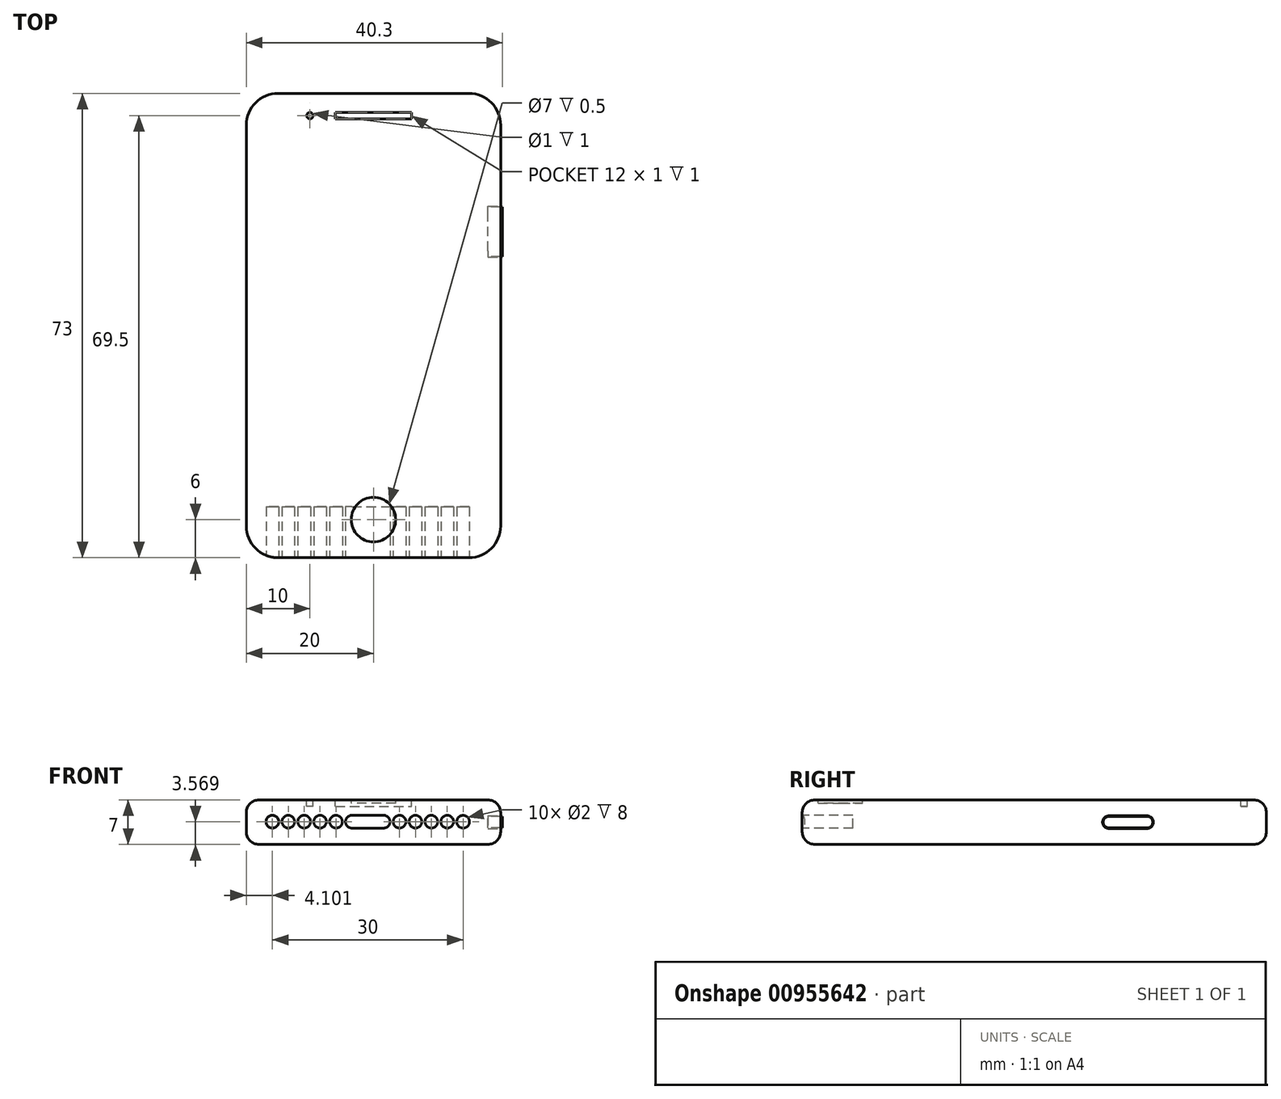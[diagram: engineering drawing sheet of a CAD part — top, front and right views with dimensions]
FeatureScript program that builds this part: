
annotation { "Feature Type Name" : "Feature", "Feature Type Description" : "" }
export const myFeature = defineFeature(function(context is Context, id is Id, definition is map)
    precondition{}
    {
        {
            var Q0;
            Q0=qCreatedBy(makeId("Top.planeOp"),FACE);
            var sketch = newSketch(context, id + "F0", { "sketchPlane" : qUnion([Q0])});
            skLineSegment(sketch, "E0.bottom", {"start": v(0, 0) * mm, "end": v(40, 0) * mm});
            skLineSegment(sketch, "E0.top", {"start": v(0, 73) * mm, "end": v(40, 73) * mm});
            skLineSegment(sketch, "E0.left", {"start": v(0, 0) * mm, "end": v(0, 73) * mm});
            skLineSegment(sketch, "E0.right", {"start": v(40, 0) * mm, "end": v(40, 73) * mm});
            skSolve(sketch);
        }
        {
            var Q0;
            Q0=makeQuery(id+"F0.imprint","IMPRINT",FACE,{"disambiguationData":[TD([[makeQuery(id+"F0.imprint","IMPRINT",EDGE,{"derivedFrom":sQuery(id+"F0.wireOp",EDGE,"E0.bottom")}),1.0]])]});
            extrude(context, id + "F1", {"entities" : qUnion([Q0]), "depth" : 7 * mm, "offsetDistance" : 25 * mm});
        }
        {
            var Q0;
            Q0=makeQuery(id+"F1.opExtrude","SWEPT_FACE",FACE,{"disambiguationData":[OSD([sQuery(id+"F0.wireOp",EDGE,"E0.bottom")])]});
            var sketch = newSketch(context, id + "F2", { "sketchPlane" : qUnion([Q0])});
            skLineSegment(sketch, "E1", {"start": v(0, 3.5) * mm, "end": v(40, 3.5) * mm});
            skSolve(sketch);
        }
        {
            var Q0;
            {var subQ0=sQuery(id+"F2.wireOp",EDGE,"E1");Q0=makeQuery(id+"F2.imprint","IMPRINT",FACE,{"disambiguationData":[TD([[makeQuery(id+"F2.imprint","IMPRINT",EDGE,{"derivedFrom":subQ0}),1.0]])]});}
            var sketch = newSketch(context, id + "F3", { "sketchPlane" : qUnion([Q0])});
            skCircle(sketch, "E2", {"center": v(4.1, 3.57) * mm, "radius": 1 * mm});
            skCircle(sketch, "E3.1.0.0", {"center": v(6.6, 3.57) * mm, "radius": 1 * mm});
            skCircle(sketch, "E3.2.0.0", {"center": v(9.1, 3.57) * mm, "radius": 1 * mm});
            skCircle(sketch, "E3.3.0.0", {"center": v(11.6, 3.57) * mm, "radius": 1 * mm});
            skCircle(sketch, "E3.4.0.0", {"center": v(14.1, 3.57) * mm, "radius": 1 * mm});
            skArc(sketch, "E3.5.0.0", {"start": v(16.6, 4.57) * mm, "mid": v(15.6, 3.57) * mm, "end": v(16.6, 2.57) * mm});
            skArc(sketch, "E3.7.0.0", {"start": v(21.6, 2.57) * mm, "mid": v(22.6, 3.57) * mm, "end": v(21.6, 4.57) * mm});
            skCircle(sketch, "E3.8.0.0", {"center": v(24.1, 3.57) * mm, "radius": 1 * mm});
            skCircle(sketch, "E3.9.0.0", {"center": v(26.6, 3.57) * mm, "radius": 1 * mm});
            skCircle(sketch, "E3.10.0.0", {"center": v(29.1, 3.57) * mm, "radius": 1 * mm});
            skCircle(sketch, "E3.11.0.0", {"center": v(31.6, 3.57) * mm, "radius": 1 * mm});
            skCircle(sketch, "E3.12.0.0", {"center": v(34.1, 3.57) * mm, "radius": 1 * mm});
            skLineSegment(sketch, "E3.direction1", {"start": v(4.1, 3.57) * mm, "end": v(6.6, 3.57) * mm, "construction": true});
            skLineSegment(sketch, "E4.bottom", {"start": v(16.6, 4.57) * mm, "end": v(21.6, 4.57) * mm});
            skLineSegment(sketch, "E4.top", {"start": v(16.6, 2.57) * mm, "end": v(21.6, 2.57) * mm});
            skSolve(sketch);
        }
        {
            var Q0;
            Q0 = qSketchRegion(id + "F3", true);
            extrude(context, id + "F4", {"entities" : qUnion([Q0]), "operationType" : NewBodyOperationType.REMOVE, "oppositeDirection" : true, "depth" : 8 * mm, "offsetDistance" : 25 * mm});
        }
        {
            var Q0;
            Q0=makeQuery(id+"F1.opExtrude","SWEPT_FACE",FACE,{"disambiguationData":[OSD([sQuery(id+"F0.wireOp",EDGE,"E0.right")])]});
            var sketch = newSketch(context, id + "F5", { "sketchPlane" : qUnion([Q0])});
            skLineSegment(sketch, "E5", {"start": v(0, 3.5) * mm, "end": v(73, 3.5) * mm, "construction": true});
            skArc(sketch, "E6", {"start": v(48.24, 4.5) * mm, "mid": v(47.24, 3.5) * mm, "end": v(48.24, 2.5) * mm});
            skArc(sketch, "E7.1.0.0", {"start": v(54.24, 2.5) * mm, "mid": v(55.24, 3.5) * mm, "end": v(54.24, 4.5) * mm});
            skLineSegment(sketch, "E7.direction1", {"start": v(48.24, 3.5) * mm, "end": v(54.24, 3.5) * mm, "construction": true});
            skLineSegment(sketch, "E8.bottom", {"start": v(48.24, 4.5) * mm, "end": v(54.24, 4.5) * mm});
            skLineSegment(sketch, "E8.top", {"start": v(48.24, 2.5) * mm, "end": v(54.24, 2.5) * mm});
            skSolve(sketch);
        }
        {
            var Q0;
            Q0=makeQuery(id+"F5.imprint","IMPRINT",FACE,{"disambiguationData":[TD([[makeQuery(id+"F5.imprint","IMPRINT",EDGE,{"derivedFrom":sQuery(id+"F5.wireOp",EDGE,"E6")}),1.0]])]});
            extrude(context, id + "F6", {"entities" : qUnion([Q0]), "operationType" : NewBodyOperationType.REMOVE, "oppositeDirection" : true, "depth" : 2 * mm, "offsetDistance" : 25 * mm});
        }
        {
            var Q0;
            Q0=makeQuery(id+"F6.boolean.opBoolean","COPY",FACE,{"derivedFrom":makeQuery(id+"F6.opExtrude","CAP_FACE",FACE,{"disambiguationData":[OSD([sQuery(id+"F5.wireOp",EDGE,"E6"),sQuery(id+"F5.wireOp",EDGE,"E7.1.0.0"),sQuery(id+"F5.wireOp",EDGE,"E8.bottom"),sQuery(id+"F5.wireOp",EDGE,"E8.top")])],"isStart":false})});
            var sketch = newSketch(context, id + "F7", { "sketchPlane" : qUnion([Q0])});
            skArc(sketch, "E9", {"start": v(48.24, 4.4) * mm, "mid": v(47.34, 3.5) * mm, "end": v(48.24, 2.6) * mm});
            skArc(sketch, "E10.1.0.0", {"start": v(54.24, 2.6) * mm, "mid": v(55.14, 3.5) * mm, "end": v(54.24, 4.4) * mm});
            skLineSegment(sketch, "E11.bottom", {"start": v(48.24, 4.4) * mm, "end": v(54.24, 4.4) * mm});
            skLineSegment(sketch, "E11.top", {"start": v(48.24, 2.6) * mm, "end": v(54.24, 2.6) * mm});
            skSolve(sketch);
        }
        {
            var Q0;
            Q0 = qSketchRegion(id + "F7", true);
            extrude(context, id + "F8", {"entities" : qUnion([Q0]), "operationType" : NewBodyOperationType.ADD, "depth" : 2.3 * mm, "offsetDistance" : 25 * mm});
        }
        {
            var Q0;
            Q0=makeQuery(id+"F1.opExtrude","CAP_FACE",FACE,{"disambiguationData":[OSD([sQuery(id+"F0.wireOp",EDGE,"E0.bottom"),sQuery(id+"F0.wireOp",EDGE,"E0.top"),sQuery(id+"F0.wireOp",EDGE,"E0.left"),sQuery(id+"F0.wireOp",EDGE,"E0.right")])],"isStart":false});
            var sketch = newSketch(context, id + "F9", { "sketchPlane" : qUnion([Q0])});
            skCircle(sketch, "E12", {"center": v(20, 6) * mm, "radius": 3.5 * mm});
            skSolve(sketch);
        }
        {
            var Q0;
            Q0 = qSketchRegion(id + "F9", true);
            extrude(context, id + "F10", {"entities" : qUnion([Q0]), "operationType" : NewBodyOperationType.REMOVE, "oppositeDirection" : true, "depth" : 0.5 * mm, "offsetDistance" : 25 * mm});
        }
        {
            var Q0;
            Q0=makeQuery(id+"F1.opExtrude","CAP_FACE",FACE,{"disambiguationData":[OSD([sQuery(id+"F0.wireOp",EDGE,"E0.bottom"),sQuery(id+"F0.wireOp",EDGE,"E0.top"),sQuery(id+"F0.wireOp",EDGE,"E0.left"),sQuery(id+"F0.wireOp",EDGE,"E0.right")])],"isStart":false});
            var sketch = newSketch(context, id + "F11", { "sketchPlane" : qUnion([Q0])});
            skLineSegment(sketch, "E13", {"start": v(20, 70) * mm, "end": v(20, 69) * mm, "construction": true});
            skLineSegment(sketch, "E14", {"start": v(14, 70) * mm, "end": v(26, 70) * mm});
            skLineSegment(sketch, "E15.top", {"start": v(14, 69) * mm, "end": v(26, 69) * mm});
            skLineSegment(sketch, "E15.left", {"start": v(14, 70) * mm, "end": v(14, 69) * mm});
            skLineSegment(sketch, "E15.right", {"start": v(26, 70) * mm, "end": v(26, 69) * mm});
            skPoint(sketch, "E16.orphan", {"position": v(20, 73) * mm});
            skLineSegment(sketch, "E17.right", {"start": v(10, 70) * mm, "end": v(10, 69) * mm});
            skCircle(sketch, "E18", {"center": v(10, 69.5) * mm, "radius": 0.5 * mm});
            skLineSegment(sketch, "E19.trimOffspring", {"start": v(14, 69) * mm, "end": v(26, 69) * mm, "construction": true});
            skPoint(sketch, "E20.start.orphan", {"position": v(0, 69) * mm});
            skPoint(sketch, "E21.orphan", {"position": v(40, 69) * mm});
            skSolve(sketch);
        }
        {
            var Q0;
            Q0 = qSketchRegion(id + "F11", true);
            extrude(context, id + "F12", {"entities" : qUnion([Q0]), "operationType" : NewBodyOperationType.REMOVE, "oppositeDirection" : true, "depth" : 1 * mm, "offsetDistance" : 25 * mm});
        }
        {
            var Q0;
            Q0=makeQuery(id+"F1.opExtrude","SWEPT_EDGE",EDGE,{"disambiguationData":[OSD([sQuery(id+"F0.wireOp",EDGE,"E0.bottom"),sQuery(id+"F0.wireOp",EDGE,"E0.right")])]});
            var Q1;
            Q1=makeQuery(id+"F1.opExtrude","SWEPT_EDGE",EDGE,{"disambiguationData":[OSD([sQuery(id+"F0.wireOp",EDGE,"E0.bottom"),sQuery(id+"F0.wireOp",EDGE,"E0.left")])]});
            var Q2;
            Q2=makeQuery(id+"F1.opExtrude","SWEPT_EDGE",EDGE,{"disambiguationData":[OSD([sQuery(id+"F0.wireOp",EDGE,"E0.top"),sQuery(id+"F0.wireOp",EDGE,"E0.right")])]});
            var Q3;
            Q3=makeQuery(id+"F1.opExtrude","SWEPT_EDGE",EDGE,{"disambiguationData":[OSD([sQuery(id+"F0.wireOp",EDGE,"E0.top"),sQuery(id+"F0.wireOp",EDGE,"E0.left")])]});
            fillet(context, id + "F13", {"entities" : qUnion([Q0, Q1, Q2, Q3]), "radius" : 5 * mm, "tangentPropagation" : true, "allowEdgeOverflow" : false});
        }
        {
            var Q0;
            {var subQ0=sQuery(id+"F0.wireOp",EDGE,"E0.right");var subQ1=sQuery(id+"F0.wireOp",EDGE,"E0.top");Q0=makeQuery(id+"F13.opFillet","BLEND_EDGE",EDGE,{"blendedFrom":[makeQuery(id+"F1.opExtrude","SWEPT_EDGE",EDGE,{"disambiguationData":[OSD([subQ1,subQ0])]}),makeQuery(id+"F1.opExtrude","CAP_FACE",FACE,{"disambiguationData":[OSD([sQuery(id+"F0.wireOp",EDGE,"E0.bottom"),subQ1,sQuery(id+"F0.wireOp",EDGE,"E0.left"),subQ0])],"isStart":false})],"blendedInto":[makeQuery(id+"F1.opExtrude","CAP_FACE",FACE,{"disambiguationData":[OSD([sQuery(id+"F0.wireOp",EDGE,"E0.bottom"),subQ1,sQuery(id+"F0.wireOp",EDGE,"E0.left"),subQ0])],"isStart":false})]});}
            var Q1;
            Q1=makeQuery(id+"F1.opExtrude","CAP_EDGE",EDGE,{"disambiguationData":[OSD([sQuery(id+"F0.wireOp",EDGE,"E0.top")])],"isStart":false});
            var Q2;
            {var subQ0=sQuery(id+"F0.wireOp",EDGE,"E0.left");var subQ1=sQuery(id+"F0.wireOp",EDGE,"E0.top");Q2=makeQuery(id+"F13.opFillet","BLEND_EDGE",EDGE,{"blendedFrom":[makeQuery(id+"F1.opExtrude","SWEPT_EDGE",EDGE,{"disambiguationData":[OSD([subQ1,subQ0])]}),makeQuery(id+"F1.opExtrude","CAP_FACE",FACE,{"disambiguationData":[OSD([sQuery(id+"F0.wireOp",EDGE,"E0.bottom"),subQ1,subQ0,sQuery(id+"F0.wireOp",EDGE,"E0.right")])],"isStart":false})],"blendedInto":[makeQuery(id+"F1.opExtrude","CAP_FACE",FACE,{"disambiguationData":[OSD([sQuery(id+"F0.wireOp",EDGE,"E0.bottom"),subQ1,subQ0,sQuery(id+"F0.wireOp",EDGE,"E0.right")])],"isStart":false})]});}
            var Q3;
            Q3=makeQuery(id+"F1.opExtrude","CAP_EDGE",EDGE,{"disambiguationData":[OSD([sQuery(id+"F0.wireOp",EDGE,"E0.left")])],"isStart":false});
            var Q4;
            {var subQ0=sQuery(id+"F0.wireOp",EDGE,"E0.left");var subQ1=sQuery(id+"F0.wireOp",EDGE,"E0.bottom");Q4=makeQuery(id+"F13.opFillet","BLEND_EDGE",EDGE,{"blendedFrom":[makeQuery(id+"F1.opExtrude","SWEPT_EDGE",EDGE,{"disambiguationData":[OSD([subQ1,subQ0])]}),makeQuery(id+"F1.opExtrude","CAP_FACE",FACE,{"disambiguationData":[OSD([subQ1,sQuery(id+"F0.wireOp",EDGE,"E0.top"),subQ0,sQuery(id+"F0.wireOp",EDGE,"E0.right")])],"isStart":false})],"blendedInto":[makeQuery(id+"F1.opExtrude","CAP_FACE",FACE,{"disambiguationData":[OSD([subQ1,sQuery(id+"F0.wireOp",EDGE,"E0.top"),subQ0,sQuery(id+"F0.wireOp",EDGE,"E0.right")])],"isStart":false})]});}
            var Q5;
            Q5=makeQuery(id+"F1.opExtrude","CAP_EDGE",EDGE,{"disambiguationData":[OSD([sQuery(id+"F0.wireOp",EDGE,"E0.bottom")])],"isStart":false});
            var Q6;
            {var subQ0=sQuery(id+"F0.wireOp",EDGE,"E0.right");var subQ1=sQuery(id+"F0.wireOp",EDGE,"E0.bottom");Q6=makeQuery(id+"F13.opFillet","BLEND_EDGE",EDGE,{"blendedFrom":[makeQuery(id+"F1.opExtrude","SWEPT_EDGE",EDGE,{"disambiguationData":[OSD([subQ1,subQ0])]}),makeQuery(id+"F1.opExtrude","CAP_FACE",FACE,{"disambiguationData":[OSD([subQ1,sQuery(id+"F0.wireOp",EDGE,"E0.top"),sQuery(id+"F0.wireOp",EDGE,"E0.left"),subQ0])],"isStart":false})],"blendedInto":[makeQuery(id+"F1.opExtrude","CAP_FACE",FACE,{"disambiguationData":[OSD([subQ1,sQuery(id+"F0.wireOp",EDGE,"E0.top"),sQuery(id+"F0.wireOp",EDGE,"E0.left"),subQ0])],"isStart":false})]});}
            var Q7;
            Q7=makeQuery(id+"F1.opExtrude","CAP_EDGE",EDGE,{"disambiguationData":[OSD([sQuery(id+"F0.wireOp",EDGE,"E0.right")])],"isStart":false});
            fillet(context, id + "F14", {"entities" : qUnion([Q0, Q1, Q2, Q3, Q4, Q5, Q6, Q7]), "radius" : 2 * mm, "tangentPropagation" : true, "allowEdgeOverflow" : false});
        }
        {
            var Q0;
            Q0=makeQuery(id+"F1.opExtrude","CAP_EDGE",EDGE,{"disambiguationData":[OSD([sQuery(id+"F0.wireOp",EDGE,"E0.right")])],"isStart":true});
            var Q1;
            {var subQ0=sQuery(id+"F0.wireOp",EDGE,"E0.right");var subQ1=sQuery(id+"F0.wireOp",EDGE,"E0.top");Q1=makeQuery(id+"F13.opFillet","BLEND_EDGE",EDGE,{"blendedFrom":[makeQuery(id+"F1.opExtrude","SWEPT_EDGE",EDGE,{"disambiguationData":[OSD([subQ1,subQ0])]}),makeQuery(id+"F1.opExtrude","CAP_FACE",FACE,{"disambiguationData":[OSD([sQuery(id+"F0.wireOp",EDGE,"E0.bottom"),subQ1,sQuery(id+"F0.wireOp",EDGE,"E0.left"),subQ0])],"isStart":true})],"blendedInto":[makeQuery(id+"F1.opExtrude","CAP_FACE",FACE,{"disambiguationData":[OSD([sQuery(id+"F0.wireOp",EDGE,"E0.bottom"),subQ1,sQuery(id+"F0.wireOp",EDGE,"E0.left"),subQ0])],"isStart":true})]});}
            var Q2;
            Q2=makeQuery(id+"F1.opExtrude","CAP_EDGE",EDGE,{"disambiguationData":[OSD([sQuery(id+"F0.wireOp",EDGE,"E0.top")])],"isStart":true});
            var Q3;
            {var subQ0=sQuery(id+"F0.wireOp",EDGE,"E0.left");var subQ1=sQuery(id+"F0.wireOp",EDGE,"E0.top");Q3=makeQuery(id+"F13.opFillet","BLEND_EDGE",EDGE,{"blendedFrom":[makeQuery(id+"F1.opExtrude","SWEPT_EDGE",EDGE,{"disambiguationData":[OSD([subQ1,subQ0])]}),makeQuery(id+"F1.opExtrude","CAP_FACE",FACE,{"disambiguationData":[OSD([sQuery(id+"F0.wireOp",EDGE,"E0.bottom"),subQ1,subQ0,sQuery(id+"F0.wireOp",EDGE,"E0.right")])],"isStart":true})],"blendedInto":[makeQuery(id+"F1.opExtrude","CAP_FACE",FACE,{"disambiguationData":[OSD([sQuery(id+"F0.wireOp",EDGE,"E0.bottom"),subQ1,subQ0,sQuery(id+"F0.wireOp",EDGE,"E0.right")])],"isStart":true})]});}
            var Q4;
            Q4=makeQuery(id+"F1.opExtrude","CAP_EDGE",EDGE,{"disambiguationData":[OSD([sQuery(id+"F0.wireOp",EDGE,"E0.left")])],"isStart":true});
            var Q5;
            {var subQ0=sQuery(id+"F0.wireOp",EDGE,"E0.right");var subQ1=sQuery(id+"F0.wireOp",EDGE,"E0.bottom");Q5=makeQuery(id+"F13.opFillet","BLEND_EDGE",EDGE,{"blendedFrom":[makeQuery(id+"F1.opExtrude","SWEPT_EDGE",EDGE,{"disambiguationData":[OSD([subQ1,subQ0])]}),makeQuery(id+"F1.opExtrude","CAP_FACE",FACE,{"disambiguationData":[OSD([subQ1,sQuery(id+"F0.wireOp",EDGE,"E0.top"),sQuery(id+"F0.wireOp",EDGE,"E0.left"),subQ0])],"isStart":true})],"blendedInto":[makeQuery(id+"F1.opExtrude","CAP_FACE",FACE,{"disambiguationData":[OSD([subQ1,sQuery(id+"F0.wireOp",EDGE,"E0.top"),sQuery(id+"F0.wireOp",EDGE,"E0.left"),subQ0])],"isStart":true})]});}
            var Q6;
            Q6=makeQuery(id+"F1.opExtrude","CAP_EDGE",EDGE,{"disambiguationData":[OSD([sQuery(id+"F0.wireOp",EDGE,"E0.bottom")])],"isStart":true});
            var Q7;
            {var subQ0=sQuery(id+"F0.wireOp",EDGE,"E0.left");var subQ1=sQuery(id+"F0.wireOp",EDGE,"E0.bottom");Q7=makeQuery(id+"F13.opFillet","BLEND_EDGE",EDGE,{"blendedFrom":[makeQuery(id+"F1.opExtrude","SWEPT_EDGE",EDGE,{"disambiguationData":[OSD([subQ1,subQ0])]}),makeQuery(id+"F1.opExtrude","CAP_FACE",FACE,{"disambiguationData":[OSD([subQ1,sQuery(id+"F0.wireOp",EDGE,"E0.top"),subQ0,sQuery(id+"F0.wireOp",EDGE,"E0.right")])],"isStart":true})],"blendedInto":[makeQuery(id+"F1.opExtrude","CAP_FACE",FACE,{"disambiguationData":[OSD([subQ1,sQuery(id+"F0.wireOp",EDGE,"E0.top"),subQ0,sQuery(id+"F0.wireOp",EDGE,"E0.right")])],"isStart":true})]});}
            fillet(context, id + "F15", {"entities" : qUnion([Q0, Q1, Q2, Q3, Q4, Q5, Q6, Q7]), "radius" : 2 * mm, "tangentPropagation" : true, "allowEdgeOverflow" : false});
        }
    });
